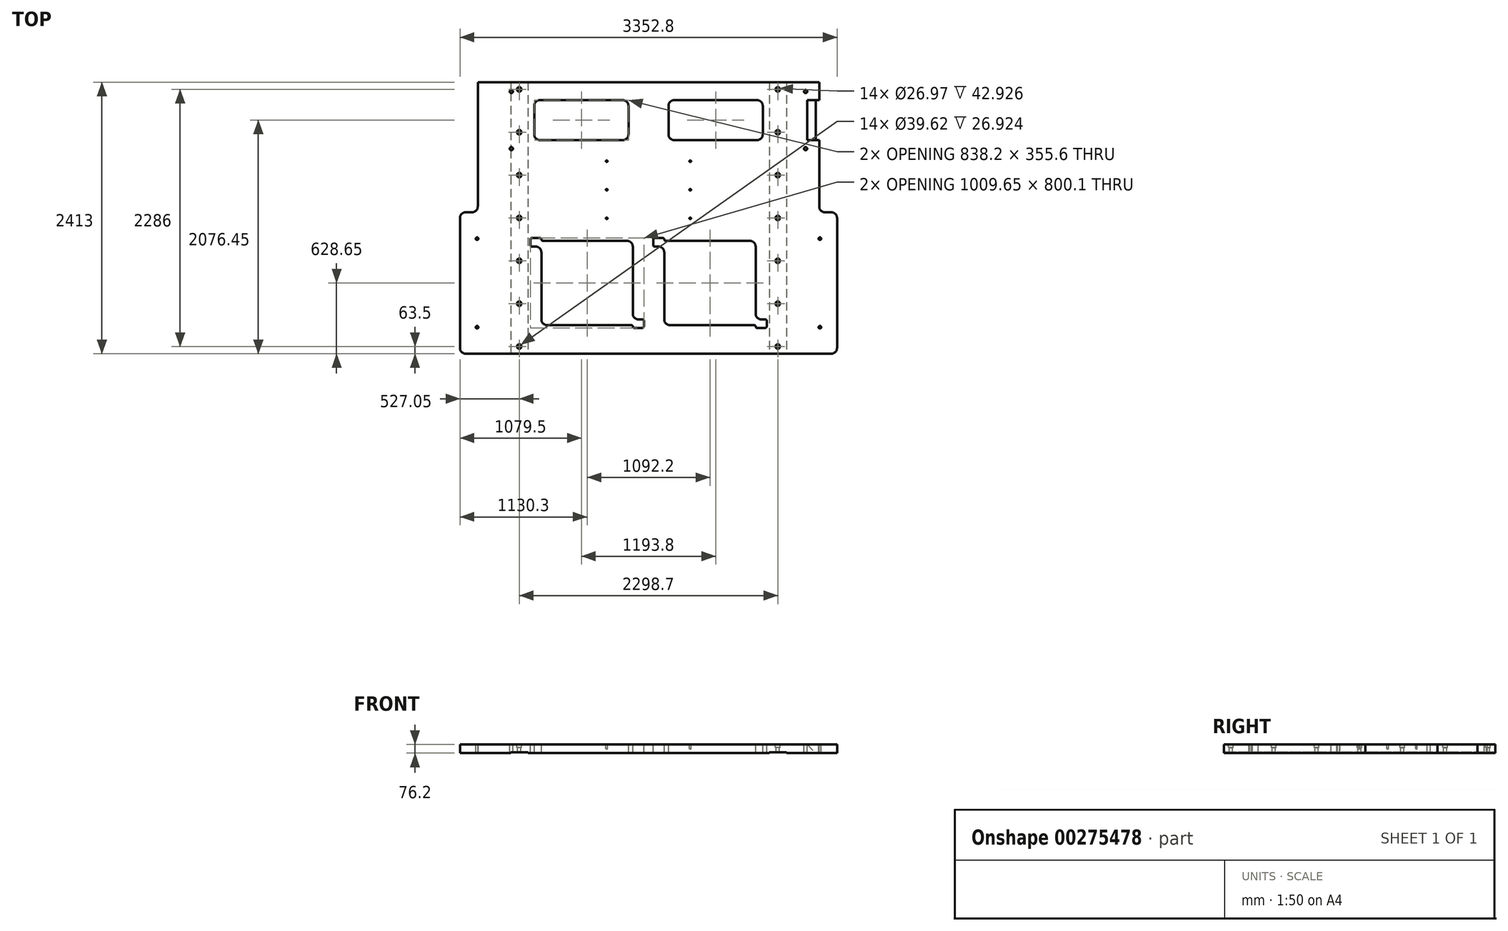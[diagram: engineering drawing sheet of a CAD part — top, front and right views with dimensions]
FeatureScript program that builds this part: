
annotation { "Feature Type Name" : "Feature", "Feature Type Description" : "" }
export const myFeature = defineFeature(function(context is Context, id is Id, definition is map)
    precondition{}
    {
        {
            var Q0;
            Q0=qCreatedBy(makeId("Top.planeOp"),FACE);
            var sketch = newSketch(context, id + "F0", { "sketchPlane" : qUnion([Q0])});
            skLineSegment(sketch, "E0.bottom", {"start": v(-1676.4, 1206.5) * mm, "end": v(1676.4, 1206.5) * mm});
            skLineSegment(sketch, "E0.top", {"start": v(-1676.4, -1206.5) * mm, "end": v(1676.4, -1206.5) * mm});
            skLineSegment(sketch, "E0.left", {"start": v(-1676.4, 1206.5) * mm, "end": v(-1676.4, -1206.5) * mm});
            skLineSegment(sketch, "E0.right", {"start": v(1676.4, 1206.5) * mm, "end": v(1676.4, -1206.5) * mm});
            skPoint(sketch, "E0.middle", {"position": v(0, 0) * mm});
            skSolve(sketch);
        }
        {
            var Q0;
            Q0 = qSketchRegion(id + "F0", true);
            extrude(context, id + "F1", {"entities" : qUnion([Q0]), "oppositeDirection" : true, "depth" : 76.2 * mm});
        }
        {
            var Q0;
            Q0=makeQuery(id+"F1.opExtrude","SWEPT_FACE",FACE,{"disambiguationData":[OSD([sQuery(id+"F0.wireOp",EDGE,"E0.top")])]});
            var sketch = newSketch(context, id + "F2", { "sketchPlane" : qUnion([Q0])});
            skLineSegment(sketch, "E1", {"start": v(0, 468.94) * mm, "end": v(0, -416.44) * mm, "construction": true});
            skLineSegment(sketch, "E2.0", {"start": v(-1676.4, -76.2) * mm, "end": v(1676.4, -76.2) * mm, "construction": true});
            skLineSegment(sketch, "E3.0", {"start": v(-1073.15, 468.94) * mm, "end": v(-1073.15, -416.44) * mm, "construction": true});
            skLineSegment(sketch, "E4.0", {"start": v(-1517.65, -69.85) * mm, "end": v(1517.65, -69.85) * mm, "construction": true});
            skLineSegment(sketch, "E5.bottom", {"start": v(-1073.15, -69.85) * mm, "end": v(-1225.55, -69.85) * mm});
            skLineSegment(sketch, "E5.top", {"start": v(-1073.15, -95.25) * mm, "end": v(-1225.55, -95.25) * mm});
            skLineSegment(sketch, "E5.left", {"start": v(-1073.15, -69.85) * mm, "end": v(-1073.15, -95.25) * mm});
            skLineSegment(sketch, "E5.right", {"start": v(-1225.55, -69.85) * mm, "end": v(-1225.55, -95.25) * mm});
            skLineSegment(sketch, "E6.MirrorCS", {"start": v(1073.15, -69.85) * mm, "end": v(1073.15, -95.25) * mm});
            skLineSegment(sketch, "E7.MirrorCS", {"start": v(1225.55, -69.85) * mm, "end": v(1225.55, -95.25) * mm});
            skLineSegment(sketch, "E8.MirrorCS", {"start": v(1073.15, -95.25) * mm, "end": v(1225.55, -95.25) * mm});
            skLineSegment(sketch, "E9.MirrorCS", {"start": v(1073.15, -69.85) * mm, "end": v(1225.55, -69.85) * mm});
            skSolve(sketch);
        }
        {
            var Q0;
            {var subQ0=sQuery(id+"F2.wireOp",EDGE,"E5.top");Q0=makeQuery(id+"F2.imprint","IMPRINT",FACE,{"disambiguationData":[TD([[makeQuery(id+"F2.imprint","IMPRINT",EDGE,{"derivedFrom":subQ0}),-1.0]])]});}
            var Q1;
            {var subQ0=sQuery(id+"F2.wireOp",EDGE,"E8.MirrorCS");Q1=makeQuery(id+"F2.imprint","IMPRINT",FACE,{"disambiguationData":[TD([[makeQuery(id+"F2.imprint","IMPRINT",EDGE,{"derivedFrom":subQ0}),1.0]])]});}
            var Q2;
            {var subQ0=sQuery(id+"F2.wireOp",EDGE,"E9.MirrorCS");Q2=makeQuery(id+"F2.imprint","IMPRINT",FACE,{"disambiguationData":[TD([[makeQuery(id+"F2.imprint","IMPRINT",EDGE,{"derivedFrom":subQ0}),-1.0]])]});}
            var Q3;
            {var subQ0=sQuery(id+"F2.wireOp",EDGE,"E5.bottom");Q3=makeQuery(id+"F2.imprint","IMPRINT",FACE,{"disambiguationData":[TD([[makeQuery(id+"F2.imprint","IMPRINT",EDGE,{"derivedFrom":subQ0}),1.0]])]});}
            extrude(context, id + "F3", {"entities" : qUnion([Q0, Q1, Q2, Q3]), "operationType" : NewBodyOperationType.REMOVE, "endBound" : BoundingType.THROUGH_ALL, "oppositeDirection" : true, "depth" : 25.4 * mm});
        }
        {
            var Q0;
            Q0=makeQuery(id+"F1.opExtrude","CAP_FACE",FACE,{"disambiguationData":[OSD([sQuery(id+"F0.wireOp",EDGE,"E0.bottom"),sQuery(id+"F0.wireOp",EDGE,"E0.top"),sQuery(id+"F0.wireOp",EDGE,"E0.left"),sQuery(id+"F0.wireOp",EDGE,"E0.right")])],"isStart":true});
            var sketch = newSketch(context, id + "F4", { "sketchPlane" : qUnion([Q0])});
            skLineSegment(sketch, "E10", {"start": v(0, 2002.4) * mm, "end": v(0, -1867.77) * mm, "construction": true});
            skLineSegment(sketch, "E11.0", {"start": v(-1517.65, 2002.4) * mm, "end": v(-1517.65, -1867.77) * mm, "construction": true});
            skLineSegment(sketch, "E12.0", {"start": v(-1676.4, -1206.5) * mm, "end": v(1676.4, -1206.5) * mm, "construction": true});
            skLineSegment(sketch, "E13.0", {"start": v(-1676.4, 50.8) * mm, "end": v(1676.4, 50.8) * mm, "construction": true});
            skLineSegment(sketch, "E14.0", {"start": v(-1682.75, 1212.85) * mm, "end": v(-1682.75, -1212.85) * mm, "construction": true});
            skLineSegment(sketch, "E14.1", {"start": v(1682.75, 1212.85) * mm, "end": v(-1682.75, 1212.85) * mm, "construction": true});
            skLineSegment(sketch, "E14.2", {"start": v(1682.75, -1212.85) * mm, "end": v(1682.75, 1212.85) * mm, "construction": true});
            skLineSegment(sketch, "E14.3", {"start": v(-1682.75, -1212.85) * mm, "end": v(1682.75, -1212.85) * mm, "construction": true});
            skLineSegment(sketch, "E15.bottom", {"start": v(-1517.65, 50.8) * mm, "end": v(-1682.75, 50.8) * mm});
            skLineSegment(sketch, "E15.top", {"start": v(-1517.65, 1212.85) * mm, "end": v(-1682.75, 1212.85) * mm});
            skLineSegment(sketch, "E15.left", {"start": v(-1517.65, 50.8) * mm, "end": v(-1517.65, 1212.85) * mm});
            skLineSegment(sketch, "E15.right", {"start": v(-1682.75, 50.8) * mm, "end": v(-1682.75, 1212.85) * mm});
            skLineSegment(sketch, "E16.MirrorCS", {"start": v(1517.65, 50.8) * mm, "end": v(1682.75, 50.8) * mm});
            skLineSegment(sketch, "E17.MirrorCS", {"start": v(1517.65, 1212.85) * mm, "end": v(1682.75, 1212.85) * mm});
            skLineSegment(sketch, "E18.MirrorCS", {"start": v(1682.75, 50.8) * mm, "end": v(1682.75, 1212.85) * mm});
            skLineSegment(sketch, "E19.MirrorCS", {"start": v(1517.65, 50.8) * mm, "end": v(1517.65, 1212.85) * mm});
            skSolve(sketch);
        }
        {
            var Q0;
            Q0 = qSketchRegion(id + "F4", true);
            extrude(context, id + "F5", {"entities" : qUnion([Q0]), "operationType" : NewBodyOperationType.REMOVE, "endBound" : BoundingType.THROUGH_ALL, "oppositeDirection" : true, "depth" : 25.4 * mm});
        }
        {
            var Q0;
            Q0=makeQuery(id+"F1.opExtrude","SWEPT_EDGE",EDGE,{"disambiguationData":[OSD([sQuery(id+"F0.wireOp",EDGE,"E0.top"),sQuery(id+"F0.wireOp",EDGE,"E0.left")])]});
            var Q1;
            Q1=makeQuery(id+"F5.boolean.opBoolean","INTERSECT",EDGE,{"derivedFrom":[makeQuery(id+"F1.opExtrude","SWEPT_FACE",FACE,{"disambiguationData":[OSD([sQuery(id+"F0.wireOp",EDGE,"E0.left")])]}),makeQuery(id+"F5.opExtrude","SWEPT_FACE",FACE,{"disambiguationData":[OSD([sQuery(id+"F4.wireOp",EDGE,"E15.bottom")])]})]});
            var Q2;
            Q2=makeQuery(id+"F5.boolean.opBoolean","COPY",EDGE,{"derivedFrom":makeQuery(id+"F5.opExtrude","SWEPT_EDGE",EDGE,{"disambiguationData":[OSD([sQuery(id+"F4.wireOp",EDGE,"E15.bottom"),sQuery(id+"F4.wireOp",EDGE,"E15.left")])]})});
            var Q3;
            Q3=makeQuery(id+"F5.boolean.opBoolean","COPY",EDGE,{"derivedFrom":makeQuery(id+"F5.opExtrude","SWEPT_EDGE",EDGE,{"disambiguationData":[OSD([sQuery(id+"F4.wireOp",EDGE,"E16.MirrorCS"),sQuery(id+"F4.wireOp",EDGE,"E19.MirrorCS")])]})});
            var Q4;
            Q4=makeQuery(id+"F5.boolean.opBoolean","INTERSECT",EDGE,{"derivedFrom":[makeQuery(id+"F1.opExtrude","SWEPT_FACE",FACE,{"disambiguationData":[OSD([sQuery(id+"F0.wireOp",EDGE,"E0.right")])]}),makeQuery(id+"F5.opExtrude","SWEPT_FACE",FACE,{"disambiguationData":[OSD([sQuery(id+"F4.wireOp",EDGE,"E16.MirrorCS")])]})]});
            var Q5;
            Q5=makeQuery(id+"F1.opExtrude","SWEPT_EDGE",EDGE,{"disambiguationData":[OSD([sQuery(id+"F0.wireOp",EDGE,"E0.top"),sQuery(id+"F0.wireOp",EDGE,"E0.right")])]});
            fillet(context, id + "F6", {"entities" : qUnion([Q0, Q1, Q2, Q3, Q4, Q5]), "radius" : 50.8 * mm, "tangentPropagation" : true, "allowEdgeOverflow" : false});
        }
        {
            var Q0;
            Q0=makeQuery(id+"F1.opExtrude","CAP_FACE",FACE,{"disambiguationData":[OSD([sQuery(id+"F0.wireOp",EDGE,"E0.bottom"),sQuery(id+"F0.wireOp",EDGE,"E0.top"),sQuery(id+"F0.wireOp",EDGE,"E0.left"),sQuery(id+"F0.wireOp",EDGE,"E0.right")])],"isStart":true});
            var sketch = newSketch(context, id + "F7", { "sketchPlane" : qUnion([Q0])});
            skLineSegment(sketch, "E20", {"start": v(0, 1658.03) * mm, "end": v(0, -1598.46) * mm, "construction": true});
            skPoint(sketch, "E20.endSnap0", {"position": v(0, -1206.5) * mm});
            skLineSegment(sketch, "E21.0", {"start": v(-1517.65, 1206.5) * mm, "end": v(1517.65, 1206.5) * mm, "construction": true});
            skLineSegment(sketch, "E22.0", {"start": v(-1517.65, 869.95) * mm, "end": v(1517.65, 869.95) * mm, "construction": true});
            skLineSegment(sketch, "E23.bottom", {"start": v(-965.2, 692.15) * mm, "end": v(-228.6, 692.15) * mm});
            skLineSegment(sketch, "E23.top", {"start": v(-965.2, 1047.75) * mm, "end": v(-228.6, 1047.75) * mm});
            skLineSegment(sketch, "E23.left", {"start": v(-1016, 742.95) * mm, "end": v(-1016, 996.95) * mm});
            skLineSegment(sketch, "E23.right", {"start": v(-177.8, 742.95) * mm, "end": v(-177.8, 996.95) * mm});
            skPoint(sketch, "E24.visualSharp", {"position": v(-1016, 1047.75) * mm});
            skArc(sketch, "E24.filletArc", {"start": v(-965.2, 1047.75) * mm, "mid": v(-1001.12, 1032.87) * mm, "end": v(-1016, 996.95) * mm});
            skPoint(sketch, "E25.visualSharp", {"position": v(-177.8, 1047.75) * mm});
            skArc(sketch, "E25.filletArc", {"start": v(-177.8, 996.95) * mm, "mid": v(-192.68, 1032.87) * mm, "end": v(-228.6, 1047.75) * mm});
            skPoint(sketch, "E26.visualSharp", {"position": v(-177.8, 692.15) * mm});
            skArc(sketch, "E26.filletArc", {"start": v(-228.6, 692.15) * mm, "mid": v(-192.68, 707.03) * mm, "end": v(-177.8, 742.95) * mm});
            skPoint(sketch, "E27.visualSharp", {"position": v(-1016, 692.15) * mm});
            skArc(sketch, "E27.filletArc", {"start": v(-1016, 742.95) * mm, "mid": v(-1001.12, 707.03) * mm, "end": v(-965.2, 692.15) * mm});
            skArc(sketch, "E28.MirrorCS", {"start": v(1016, 742.95) * mm, "mid": v(1001.12, 707.03) * mm, "end": v(965.2, 692.15) * mm});
            skArc(sketch, "E29.MirrorCS", {"start": v(228.6, 692.15) * mm, "mid": v(192.68, 707.03) * mm, "end": v(177.8, 742.95) * mm});
            skArc(sketch, "E30.MirrorCS", {"start": v(177.8, 996.95) * mm, "mid": v(192.68, 1032.87) * mm, "end": v(228.6, 1047.75) * mm});
            skArc(sketch, "E31.MirrorCS", {"start": v(965.2, 1047.75) * mm, "mid": v(1001.12, 1032.87) * mm, "end": v(1016, 996.95) * mm});
            skPoint(sketch, "E32.MirrorP", {"position": v(177.8, 1047.75) * mm});
            skPoint(sketch, "E33.MirrorP", {"position": v(177.8, 692.15) * mm});
            skLineSegment(sketch, "E34.MirrorCS", {"start": v(965.2, 692.15) * mm, "end": v(228.6, 692.15) * mm});
            skPoint(sketch, "E35.MirrorP", {"position": v(1016, 1047.75) * mm});
            skPoint(sketch, "E36.MirrorP", {"position": v(1016, 692.15) * mm});
            skLineSegment(sketch, "E37.MirrorCS", {"start": v(177.8, 742.95) * mm, "end": v(177.8, 996.95) * mm});
            skLineSegment(sketch, "E38.MirrorCS", {"start": v(1016, 742.95) * mm, "end": v(1016, 996.95) * mm});
            skLineSegment(sketch, "E39.MirrorCS", {"start": v(965.2, 1047.75) * mm, "end": v(228.6, 1047.75) * mm});
            skSolve(sketch);
        }
        {
            var Q0;
            Q0 = qSketchRegion(id + "F7", true);
            extrude(context, id + "F8", {"entities" : qUnion([Q0]), "operationType" : NewBodyOperationType.REMOVE, "endBound" : BoundingType.THROUGH_ALL, "oppositeDirection" : true, "depth" : 25.4 * mm});
        }
        {
            var Q0;
            Q0=makeQuery(id+"F1.opExtrude","CAP_FACE",FACE,{"disambiguationData":[OSD([sQuery(id+"F0.wireOp",EDGE,"E0.bottom"),sQuery(id+"F0.wireOp",EDGE,"E0.top"),sQuery(id+"F0.wireOp",EDGE,"E0.left"),sQuery(id+"F0.wireOp",EDGE,"E0.right")])],"isStart":true});
            var sketch = newSketch(context, id + "F9", { "sketchPlane" : qUnion([Q0])});
            skLineSegment(sketch, "E40", {"start": v(0, 1573.8) * mm, "end": v(0, -1474.82) * mm, "construction": true});
            skLineSegment(sketch, "E41.0", {"start": v(-1625.6, -1206.5) * mm, "end": v(1625.6, -1206.5) * mm, "construction": true});
            skLineSegment(sketch, "E42.0", {"start": v(-1625.6, -577.85) * mm, "end": v(1625.6, -577.85) * mm, "construction": true});
            skLineSegment(sketch, "E43.0", {"start": v(-952.5, 1573.8) * mm, "end": v(-952.5, -177.8) * mm, "construction": true});
            skLineSegment(sketch, "E44.0", {"start": v(-139.7, -952.5) * mm, "end": v(0, -952.5) * mm, "construction": true});
            skLineSegment(sketch, "E45.bottom", {"start": v(-901.7, -952.5) * mm, "end": v(-152.4, -952.5) * mm});
            skLineSegment(sketch, "E45.top", {"start": v(-939.8, -203.2) * mm, "end": v(-190.5, -203.2) * mm});
            skLineSegment(sketch, "E45.left", {"start": v(-952.5, -901.7) * mm, "end": v(-952.5, -304.8) * mm});
            skLineSegment(sketch, "E45.right", {"start": v(-139.7, -850.9) * mm, "end": v(-139.7, -254) * mm});
            skLineSegment(sketch, "E46.bottom", {"start": v(-1038.22, -177.8) * mm, "end": v(-965.2, -177.8) * mm});
            skLineSegment(sketch, "E46.top", {"start": v(-1038.22, -254) * mm, "end": v(-1003.3, -254) * mm});
            skLineSegment(sketch, "E46.left", {"start": v(-1050.92, -190.5) * mm, "end": v(-1050.92, -241.3) * mm});
            skLineSegment(sketch, "E46.right", {"start": v(-952.5, -190.5) * mm, "end": v(-952.5, -190.5) * mm});
            skLineSegment(sketch, "E47", {"start": v(-546.1, -203.2) * mm, "end": v(-546.1, 0) * mm, "construction": true});
            skLineSegment(sketch, "E48.bottom", {"start": v(-53.97, -977.9) * mm, "end": v(-127, -977.9) * mm});
            skLineSegment(sketch, "E48.top", {"start": v(-53.97, -901.7) * mm, "end": v(-88.9, -901.7) * mm});
            skLineSegment(sketch, "E48.left", {"start": v(-41.27, -965.2) * mm, "end": v(-41.27, -914.4) * mm});
            skLineSegment(sketch, "E48.right", {"start": v(-139.7, -965.2) * mm, "end": v(-139.7, -965.2) * mm});
            skPoint(sketch, "E49.orphan", {"position": v(-952.5, -203.2) * mm});
            skLineSegment(sketch, "E50.trimOffspring", {"start": v(-139.7, -1004.26) * mm, "end": v(-139.7, -1474.82) * mm, "construction": true});
            skLineSegment(sketch, "E51.trimOffspring", {"start": v(-139.7, -952.5) * mm, "end": v(1625.6, -952.5) * mm, "construction": true});
            skPoint(sketch, "E52.visualSharp", {"position": v(-952.5, -952.5) * mm});
            skArc(sketch, "E52.filletArc", {"start": v(-952.5, -901.7) * mm, "mid": v(-937.62, -937.62) * mm, "end": v(-901.7, -952.5) * mm});
            skPoint(sketch, "E53.visualSharp", {"position": v(-139.7, -203.2) * mm});
            skArc(sketch, "E53.filletArc", {"start": v(-139.7, -254) * mm, "mid": v(-154.58, -218.08) * mm, "end": v(-190.5, -203.2) * mm});
            skPoint(sketch, "E54.visualSharp", {"position": v(-139.7, -901.7) * mm});
            skArc(sketch, "E54.filletArc", {"start": v(-139.7, -850.9) * mm, "mid": v(-124.82, -886.82) * mm, "end": v(-88.9, -901.7) * mm});
            skPoint(sketch, "E55.visualSharp", {"position": v(-952.5, -254) * mm});
            skArc(sketch, "E55.filletArc", {"start": v(-952.5, -304.8) * mm, "mid": v(-967.38, -268.88) * mm, "end": v(-1003.3, -254) * mm});
            skPoint(sketch, "E56.visualSharp", {"position": v(-1050.92, -254) * mm});
            skArc(sketch, "E56.filletArc", {"start": v(-1050.92, -241.3) * mm, "mid": v(-1047.2, -250.28) * mm, "end": v(-1038.22, -254) * mm});
            skPoint(sketch, "E57.visualSharp", {"position": v(-1050.92, -177.8) * mm});
            skArc(sketch, "E57.filletArc", {"start": v(-1038.22, -177.8) * mm, "mid": v(-1047.2, -181.52) * mm, "end": v(-1050.92, -190.5) * mm});
            skPoint(sketch, "E58.visualSharp", {"position": v(-952.5, -177.8) * mm});
            skArc(sketch, "E58.filletArc", {"start": v(-952.5, -190.5) * mm, "mid": v(-956.22, -181.52) * mm, "end": v(-965.2, -177.8) * mm});
            skArc(sketch, "E59.filletArc", {"start": v(-952.5, -190.5) * mm, "mid": v(-948.78, -199.48) * mm, "end": v(-939.8, -203.2) * mm});
            skPoint(sketch, "E60.visualSharp", {"position": v(-41.27, -901.7) * mm});
            skArc(sketch, "E60.filletArc", {"start": v(-41.27, -914.4) * mm, "mid": v(-45, -905.42) * mm, "end": v(-53.97, -901.7) * mm});
            skPoint(sketch, "E61.visualSharp", {"position": v(-41.27, -977.9) * mm});
            skArc(sketch, "E61.filletArc", {"start": v(-53.97, -977.9) * mm, "mid": v(-45, -974.18) * mm, "end": v(-41.27, -965.2) * mm});
            skPoint(sketch, "E62.visualSharp", {"position": v(-139.7, -977.9) * mm});
            skArc(sketch, "E62.filletArc", {"start": v(-139.7, -965.2) * mm, "mid": v(-135.98, -974.18) * mm, "end": v(-127, -977.9) * mm});
            skPoint(sketch, "E63.visualSharp", {"position": v(-139.7, -952.5) * mm});
            skArc(sketch, "E63.filletArc", {"start": v(-139.7, -965.2) * mm, "mid": v(-143.42, -956.22) * mm, "end": v(-152.4, -952.5) * mm});
            skPoint(sketch, "E64.1.0.0", {"position": v(41.28, -177.8) * mm});
            skPoint(sketch, "E64.1.0.1", {"position": v(952.5, -203.2) * mm});
            skLineSegment(sketch, "E64.1.0.2", {"start": v(139.7, -901.7) * mm, "end": v(139.7, -304.8) * mm});
            skPoint(sketch, "E64.1.0.3", {"position": v(41.28, -254) * mm});
            skLineSegment(sketch, "E64.1.0.4", {"start": v(190.5, -952.5) * mm, "end": v(939.8, -952.5) * mm});
            skLineSegment(sketch, "E64.1.0.5", {"start": v(152.4, -203.2) * mm, "end": v(901.7, -203.2) * mm});
            skLineSegment(sketch, "E64.1.0.6", {"start": v(952.5, -850.9) * mm, "end": v(952.5, -254) * mm});
            skPoint(sketch, "E64.1.0.7", {"position": v(139.7, -952.5) * mm});
            skPoint(sketch, "E64.1.0.8", {"position": v(952.5, -901.7) * mm});
            skPoint(sketch, "E64.1.0.9", {"position": v(952.5, -977.9) * mm});
            skPoint(sketch, "E64.1.0.10", {"position": v(1050.93, -977.9) * mm});
            skPoint(sketch, "E64.1.0.11", {"position": v(139.7, -177.8) * mm});
            skPoint(sketch, "E64.1.0.12", {"position": v(139.7, -254) * mm});
            skPoint(sketch, "E64.1.0.13", {"position": v(1050.93, -901.7) * mm});
            skArc(sketch, "E64.1.0.14", {"start": v(952.5, -254) * mm, "mid": v(937.62, -218.08) * mm, "end": v(901.7, -203.2) * mm});
            skArc(sketch, "E64.1.0.15", {"start": v(952.5, -850.9) * mm, "mid": v(967.38, -886.82) * mm, "end": v(1003.3, -901.7) * mm});
            skLineSegment(sketch, "E64.1.0.16", {"start": v(952.5, -952.5) * mm, "end": v(1092.2, -952.5) * mm, "construction": true});
            skPoint(sketch, "E64.1.0.17", {"position": v(139.7, -203.2) * mm});
            skPoint(sketch, "E64.1.0.18", {"position": v(952.5, -952.5) * mm});
            skLineSegment(sketch, "E64.1.0.19", {"start": v(1038.23, -977.9) * mm, "end": v(965.2, -977.9) * mm});
            skArc(sketch, "E64.1.0.20", {"start": v(139.7, -304.8) * mm, "mid": v(124.82, -268.88) * mm, "end": v(88.9, -254) * mm});
            skPoint(sketch, "E64.1.0.21", {"position": v(139.7, -203.2) * mm});
            skArc(sketch, "E64.1.0.22", {"start": v(139.7, -901.7) * mm, "mid": v(154.58, -937.62) * mm, "end": v(190.5, -952.5) * mm});
            skArc(sketch, "E64.1.0.23", {"start": v(1038.23, -977.9) * mm, "mid": v(1047.2, -974.18) * mm, "end": v(1050.93, -965.2) * mm});
            skLineSegment(sketch, "E64.1.0.24", {"start": v(53.98, -254) * mm, "end": v(88.9, -254) * mm});
            skLineSegment(sketch, "E64.1.0.25", {"start": v(53.98, -177.8) * mm, "end": v(127, -177.8) * mm});
            skLineSegment(sketch, "E64.1.0.26", {"start": v(41.28, -190.5) * mm, "end": v(41.28, -241.3) * mm});
            skArc(sketch, "E64.1.0.27", {"start": v(53.98, -177.8) * mm, "mid": v(45, -181.52) * mm, "end": v(41.28, -190.5) * mm});
            skLineSegment(sketch, "E64.1.0.28", {"start": v(1050.93, -965.2) * mm, "end": v(1050.93, -914.4) * mm});
            skLineSegment(sketch, "E64.1.0.29", {"start": v(1038.23, -901.7) * mm, "end": v(1003.3, -901.7) * mm});
            skArc(sketch, "E64.1.0.30", {"start": v(41.28, -241.3) * mm, "mid": v(45, -250.28) * mm, "end": v(53.98, -254) * mm});
            skArc(sketch, "E64.1.0.31", {"start": v(952.5, -965.2) * mm, "mid": v(948.78, -956.22) * mm, "end": v(939.8, -952.5) * mm});
            skArc(sketch, "E64.1.0.32", {"start": v(952.5, -965.2) * mm, "mid": v(956.22, -974.18) * mm, "end": v(965.2, -977.9) * mm});
            skArc(sketch, "E64.1.0.33", {"start": v(1050.93, -914.4) * mm, "mid": v(1047.2, -905.42) * mm, "end": v(1038.23, -901.7) * mm});
            skArc(sketch, "E64.1.0.34", {"start": v(139.7, -190.5) * mm, "mid": v(135.98, -181.52) * mm, "end": v(127, -177.8) * mm});
            skArc(sketch, "E64.1.0.35", {"start": v(139.7, -190.5) * mm, "mid": v(143.42, -199.48) * mm, "end": v(152.4, -203.2) * mm});
            skLineSegment(sketch, "E64.direction1", {"start": v(-952.5, -952.5) * mm, "end": v(139.7, -952.5) * mm, "construction": true});
            skSolve(sketch);
        }
        {
            var Q0;
            Q0 = qSketchRegion(id + "F9", true);
            extrude(context, id + "F10", {"entities" : qUnion([Q0]), "operationType" : NewBodyOperationType.REMOVE, "endBound" : BoundingType.THROUGH_ALL, "oppositeDirection" : true, "depth" : 25.4 * mm});
        }
        {
            var Q0;
            Q0=makeQuery(id+"F1.opExtrude","SWEPT_FACE",FACE,{"disambiguationData":[OSD([sQuery(id+"F0.wireOp",EDGE,"E0.bottom")])]});
            cPlane(context, id + "F11", {"entities" : qUnion([Q0]), "cplaneType" : CPlaneType.OFFSET, "offset" : 336.55 * mm, "oppositeDirection" : true, "width" : 152.4 * mm, "height" : 152.4 * mm});
        }
        {
            var Q0;
            Q0=qCreatedBy(id+"F11.planeOp",FACE);
            var sketch = newSketch(context, id + "F12", { "sketchPlane" : qUnion([Q0])});
            skLineSegment(sketch, "E65", {"start": v(0, 694.36) * mm, "end": v(0, -636.94) * mm, "construction": true});
            skLineSegment(sketch, "E66.0", {"start": v(-1409.7, 694.36) * mm, "end": v(-1409.7, 0) * mm, "construction": true});
            skLineSegment(sketch, "E67.0", {"start": v(-1225.55, -76.2) * mm, "end": v(-1409.7, -76.2) * mm, "construction": true});
            skLineSegment(sketch, "E68.top", {"start": v(-1409.7, 0) * mm, "end": v(-1485.91, 0) * mm});
            skLineSegment(sketch, "E69", {"start": v(-1409.7, 0) * mm, "end": v(-1485.91, -76.2) * mm});
            skLineSegment(sketch, "E70.trimOffspring", {"start": v(-1409.7, -76.2) * mm, "end": v(-1409.7, -636.94) * mm, "construction": true});
            skLineSegment(sketch, "E71.trimOffspring", {"start": v(-1485.91, -76.2) * mm, "end": v(-1517.65, -76.2) * mm, "construction": true});
            skLineSegment(sketch, "E72.bottom", {"start": v(-1485.91, 0) * mm, "end": v(-1554.1, 0) * mm});
            skLineSegment(sketch, "E72.top", {"start": v(-1485.91, -76.2) * mm, "end": v(-1554.1, -76.2) * mm});
            skLineSegment(sketch, "E72.right", {"start": v(-1554.1, 0) * mm, "end": v(-1554.1, -76.2) * mm});
            skSolve(sketch);
        }
        {
            var Q0;
            Q0 = qSketchRegion(id + "F12", true);
            extrude(context, id + "F13", {"entities" : qUnion([Q0]), "operationType" : NewBodyOperationType.REMOVE, "endBound" : BoundingType.SYMMETRIC, "oppositeDirection" : true, "depth" : 355.6 * mm});
        }
        {
            var Q0;
            Q0=makeQuery(id+"F1.opExtrude","CAP_FACE",FACE,{"disambiguationData":[OSD([sQuery(id+"F0.wireOp",EDGE,"E0.bottom"),sQuery(id+"F0.wireOp",EDGE,"E0.top"),sQuery(id+"F0.wireOp",EDGE,"E0.left"),sQuery(id+"F0.wireOp",EDGE,"E0.right")])],"isStart":true});
            var sketch = newSketch(context, id + "F14", { "sketchPlane" : qUnion([Q0])});
            skLineSegment(sketch, "E73", {"start": v(0, 1417.77) * mm, "end": v(0, -1448.45) * mm, "construction": true});
            skLineSegment(sketch, "E74", {"start": v(-177.8, 869.95) * mm, "end": v(-2109.21, 869.95) * mm, "construction": true});
            skLineSegment(sketch, "E75.0", {"start": v(-177.8, 250.7) * mm, "end": v(-2109.21, 250.7) * mm, "construction": true});
            skLineSegment(sketch, "E76.0", {"start": v(-177.8, -3.3) * mm, "end": v(-2109.21, -3.3) * mm, "construction": true});
            skLineSegment(sketch, "E77.0", {"start": v(-177.8, 504.7) * mm, "end": v(-2109.21, 504.7) * mm, "construction": true});
            skLineSegment(sketch, "E78.0", {"start": v(-371.35, 1417.77) * mm, "end": v(-371.35, -1448.45) * mm, "construction": true});
            skPoint(sketch, "E79", {"position": v(-371.35, 504.7) * mm});
            skPoint(sketch, "E80", {"position": v(-371.35, 250.7) * mm});
            skPoint(sketch, "E81", {"position": v(-371.35, -3.3) * mm});
            skPoint(sketch, "E82.MirrorP", {"position": v(371.35, 504.7) * mm});
            skPoint(sketch, "E83.MirrorP", {"position": v(371.35, 250.7) * mm});
            skPoint(sketch, "E84.MirrorP", {"position": v(371.35, -3.3) * mm});
            skSolve(sketch);
        }
        {
            var Q0;
            Q0=sQuery(id+"F14.wireOp",VERTEX,"E79");
            var Q1;
            Q1=sQuery(id+"F14.wireOp",VERTEX,"E80");
            var Q2;
            Q2=sQuery(id+"F14.wireOp",VERTEX,"E81");
            var Q3;
            Q3=sQuery(id+"F14.wireOp",VERTEX,"E82.MirrorP");
            var Q4;
            Q4=sQuery(id+"F14.wireOp",VERTEX,"E83.MirrorP");
            var Q5;
            Q5=sQuery(id+"F14.wireOp",VERTEX,"E84.MirrorP");
            var Q6;
            Q6=makeQuery(id+"F1.opExtrude","SWEPT_BODY",BODY,{"disambiguationData":[OSD([sQuery(id+"F0.wireOp",EDGE,"E0.bottom"),sQuery(id+"F0.wireOp",EDGE,"E0.top"),sQuery(id+"F0.wireOp",EDGE,"E0.left"),sQuery(id+"F0.wireOp",EDGE,"E0.right")])]});
            hole(context, id + "F15", {"style" : HoleStyle.SIMPLE, "endStyle" : HoleEndStyle.BLIND, "standardTappedOrClearance" : lookupTablePath({ "standard" : "ANSI", "engagement" : "75%", "pitch" : "11 tpi", "size" : "5/8", "type" : "Tapped" }), "standardBlindInLast" : lookupTablePath({ "standard" : "ANSI", "engagement" : "75%", "pitch" : "11 tpi", "size" : "5/8", "type" : "Tapped" }), "holeDiameter" : 13.5 * mm, "showTappedDepth" : true, "holeDepth" : 38.1 * mm, "tappedDepth" : 31.17 * mm, "tapClearance" : 3, "startFromSketch" : true, "locations" : qUnion([Q0, Q1, Q2, Q3, Q4, Q5]), "scope" : qUnion([Q6]), "majorDiameter" : 15.88 * mm});
        }
        {
            var Q0;
            Q0=makeQuery(id+"F1.opExtrude","CAP_FACE",FACE,{"disambiguationData":[OSD([sQuery(id+"F0.wireOp",EDGE,"E0.bottom"),sQuery(id+"F0.wireOp",EDGE,"E0.top"),sQuery(id+"F0.wireOp",EDGE,"E0.left"),sQuery(id+"F0.wireOp",EDGE,"E0.right")])],"isStart":true});
            var sketch = newSketch(context, id + "F16", { "sketchPlane" : qUnion([Q0])});
            skLineSegment(sketch, "E85", {"start": v(0, 1443.57) * mm, "end": v(0, -1540.72) * mm, "construction": true});
            skLineSegment(sketch, "E86.0", {"start": v(-1149.35, 1443.57) * mm, "end": v(-1149.35, -1540.72) * mm, "construction": true});
            skLineSegment(sketch, "E87.0", {"start": v(-1625.6, -1206.5) * mm, "end": v(1625.6, -1206.5) * mm, "construction": true});
            skLineSegment(sketch, "E88.0", {"start": v(-1625.6, -1143) * mm, "end": v(1625.6, -1143) * mm, "construction": true});
            skPoint(sketch, "E89", {"position": v(-1149.35, -1143) * mm});
            skPoint(sketch, "E90.0.1.0", {"position": v(-1149.35, -762) * mm});
            skPoint(sketch, "E90.0.2.0", {"position": v(-1149.35, -381) * mm});
            skPoint(sketch, "E90.0.3.0", {"position": v(-1149.35, 0) * mm});
            skPoint(sketch, "E90.0.4.0", {"position": v(-1149.35, 381) * mm});
            skPoint(sketch, "E90.0.5.0", {"position": v(-1149.35, 762) * mm});
            skPoint(sketch, "E90.0.6.0", {"position": v(-1149.35, 1143) * mm});
            skPoint(sketch, "E90.1.0.0", {"position": v(1149.35, -1143) * mm});
            skPoint(sketch, "E90.1.1.0", {"position": v(1149.35, -762) * mm});
            skPoint(sketch, "E90.1.2.0", {"position": v(1149.35, -381) * mm});
            skPoint(sketch, "E90.1.3.0", {"position": v(1149.35, 0) * mm});
            skPoint(sketch, "E90.1.4.0", {"position": v(1149.35, 381) * mm});
            skPoint(sketch, "E90.1.5.0", {"position": v(1149.35, 762) * mm});
            skPoint(sketch, "E90.1.6.0", {"position": v(1149.35, 1143) * mm});
            skLineSegment(sketch, "E90.direction1", {"start": v(-1149.35, -1143) * mm, "end": v(1149.35, -1143) * mm, "construction": true});
            skLineSegment(sketch, "E90.direction2", {"start": v(-1149.35, -1143) * mm, "end": v(-1149.35, -762) * mm, "construction": true});
            skSolve(sketch);
        }
        {
            var Q0;
            Q0=sQuery(id+"F16.wireOp",VERTEX,"E89");
            var Q1;
            Q1=sQuery(id+"F16.wireOp",VERTEX,"E90.0.1.0");
            var Q2;
            Q2=sQuery(id+"F16.wireOp",VERTEX,"E90.0.2.0");
            var Q3;
            Q3=sQuery(id+"F16.wireOp",VERTEX,"E90.0.3.0");
            var Q4;
            Q4=sQuery(id+"F16.wireOp",VERTEX,"E90.0.4.0");
            var Q5;
            Q5=sQuery(id+"F16.wireOp",VERTEX,"E90.0.5.0");
            var Q6;
            Q6=sQuery(id+"F16.wireOp",VERTEX,"E90.0.6.0");
            var Q7;
            Q7=sQuery(id+"F16.wireOp",VERTEX,"E90.1.6.0");
            var Q8;
            Q8=sQuery(id+"F16.wireOp",VERTEX,"E90.1.5.0");
            var Q9;
            Q9=sQuery(id+"F16.wireOp",VERTEX,"E90.1.4.0");
            var Q10;
            Q10=sQuery(id+"F16.wireOp",VERTEX,"E90.1.3.0");
            var Q11;
            Q11=sQuery(id+"F16.wireOp",VERTEX,"E90.1.2.0");
            var Q12;
            Q12=sQuery(id+"F16.wireOp",VERTEX,"E90.1.1.0");
            var Q13;
            Q13=sQuery(id+"F16.wireOp",VERTEX,"E90.1.0.0");
            var Q14;
            Q14=makeQuery(id+"F1.opExtrude","SWEPT_BODY",BODY,{"disambiguationData":[OSD([sQuery(id+"F0.wireOp",EDGE,"E0.bottom"),sQuery(id+"F0.wireOp",EDGE,"E0.top"),sQuery(id+"F0.wireOp",EDGE,"E0.left"),sQuery(id+"F0.wireOp",EDGE,"E0.right")])]});
            hole(context, id + "F17", {"style" : HoleStyle.C_BORE, "endStyle" : HoleEndStyle.THROUGH, "holeDiameter" : 26.97 * mm, "cBoreDiameter" : 39.62 * mm, "cBoreDepth" : 26.92 * mm, "tappedDepth" : 31.17 * mm, "tapClearance" : 3, "startFromSketch" : true, "locations" : qUnion([Q0, Q1, Q2, Q3, Q4, Q5, Q6, Q7, Q8, Q9, Q10, Q11, Q12, Q13]), "scope" : qUnion([Q14])});
        }
        {
            var Q0;
            Q0=makeQuery(id+"F1.opExtrude","CAP_FACE",FACE,{"disambiguationData":[OSD([sQuery(id+"F0.wireOp",EDGE,"E0.bottom"),sQuery(id+"F0.wireOp",EDGE,"E0.top"),sQuery(id+"F0.wireOp",EDGE,"E0.left"),sQuery(id+"F0.wireOp",EDGE,"E0.right")])],"isStart":true});
            var sketch = newSketch(context, id + "F18", { "sketchPlane" : qUnion([Q0])});
            skLineSegment(sketch, "E91", {"start": v(0, 1491.37) * mm, "end": v(0, -1763.18) * mm, "construction": true});
            skLineSegment(sketch, "E92.0", {"start": v(-1524, 1491.37) * mm, "end": v(-1524, -1763.18) * mm, "construction": true});
            skLineSegment(sketch, "E93.0", {"start": v(-1625.6, -1206.5) * mm, "end": v(1625.6, -1206.5) * mm, "construction": true});
            skLineSegment(sketch, "E94.0", {"start": v(-1625.6, -577.85) * mm, "end": v(1625.6, -577.85) * mm, "construction": true});
            skLineSegment(sketch, "E95.0", {"start": v(-1625.6, -971.55) * mm, "end": v(1625.6, -971.55) * mm, "construction": true});
            skLineSegment(sketch, "E96.0", {"start": v(-1625.6, -184.15) * mm, "end": v(1625.6, -184.15) * mm, "construction": true});
            skPoint(sketch, "E97", {"position": v(-1524, -184.15) * mm});
            skPoint(sketch, "E98", {"position": v(-1524, -971.55) * mm});
            skPoint(sketch, "E99.MirrorP", {"position": v(1524, -184.15) * mm});
            skPoint(sketch, "E100.MirrorP", {"position": v(1524, -971.55) * mm});
            skSolve(sketch);
        }
        {
            var Q0;
            Q0=sQuery(id+"F18.wireOp",VERTEX,"E97");
            var Q1;
            Q1=sQuery(id+"F18.wireOp",VERTEX,"E98");
            var Q2;
            Q2=sQuery(id+"F18.wireOp",VERTEX,"E99.MirrorP");
            var Q3;
            Q3=sQuery(id+"F18.wireOp",VERTEX,"E100.MirrorP");
            var Q4;
            Q4=makeQuery(id+"F1.opExtrude","SWEPT_BODY",BODY,{"disambiguationData":[OSD([sQuery(id+"F0.wireOp",EDGE,"E0.bottom"),sQuery(id+"F0.wireOp",EDGE,"E0.top"),sQuery(id+"F0.wireOp",EDGE,"E0.left"),sQuery(id+"F0.wireOp",EDGE,"E0.right")])]});
            hole(context, id + "F19", {"style" : HoleStyle.SIMPLE, "endStyle" : HoleEndStyle.THROUGH, "standardTappedOrClearance" : lookupTablePath({ "standard" : "ANSI", "engagement" : "75%", "pitch" : "8 tpi", "size" : "1", "type" : "Tapped" }), "standardBlindInLast" : lookupTablePath({ "standard" : "ANSI", "engagement" : "75%", "pitch" : "8 tpi", "size" : "1", "type" : "Tapped" }), "holeDiameter" : 22.22 * mm, "showTappedDepth" : true, "tappedDepth" : 31.17 * mm, "tapClearance" : 3, "startFromSketch" : true, "locations" : qUnion([Q0, Q1, Q2, Q3]), "scope" : qUnion([Q4]), "majorDiameter" : 25.4 * mm});
        }
        {
            var Q0;
            Q0=makeQuery(id+"F1.opExtrude","CAP_FACE",FACE,{"disambiguationData":[OSD([sQuery(id+"F0.wireOp",EDGE,"E0.bottom"),sQuery(id+"F0.wireOp",EDGE,"E0.top"),sQuery(id+"F0.wireOp",EDGE,"E0.left"),sQuery(id+"F0.wireOp",EDGE,"E0.right")])],"isStart":true});
            var sketch = newSketch(context, id + "F20", { "sketchPlane" : qUnion([Q0])});
            skLineSegment(sketch, "E101", {"start": v(0, 1609.78) * mm, "end": v(0, -1637.77) * mm, "construction": true});
            skLineSegment(sketch, "E102.0", {"start": v(-1517.65, 1206.5) * mm, "end": v(1517.65, 1206.5) * mm, "construction": true});
            skLineSegment(sketch, "E103.0", {"start": v(1397, 1609.78) * mm, "end": v(1397, -1637.77) * mm, "construction": true});
            skLineSegment(sketch, "E104.0", {"start": v(-1517.65, 869.95) * mm, "end": v(1517.65, 869.95) * mm, "construction": true});
            skLineSegment(sketch, "E105.0", {"start": v(-1517.65, 615.95) * mm, "end": v(1517.65, 615.95) * mm, "construction": true});
            skPoint(sketch, "E106", {"position": v(1397, 615.95) * mm});
            skPoint(sketch, "E107.MirrorP", {"position": v(1397, 1123.95) * mm});
            skSolve(sketch);
        }
        {
            var Q0;
            Q0=sQuery(id+"F20.wireOp",VERTEX,"E107.MirrorP");
            var Q1;
            Q1=sQuery(id+"F20.wireOp",VERTEX,"E106");
            var Q2;
            Q2=makeQuery(id+"F1.opExtrude","SWEPT_BODY",BODY,{"disambiguationData":[OSD([sQuery(id+"F0.wireOp",EDGE,"E0.bottom"),sQuery(id+"F0.wireOp",EDGE,"E0.top"),sQuery(id+"F0.wireOp",EDGE,"E0.left"),sQuery(id+"F0.wireOp",EDGE,"E0.right")])]});
            hole(context, id + "F21", {"style" : HoleStyle.SIMPLE, "endStyle" : HoleEndStyle.THROUGH, "standardTappedOrClearance" : lookupTablePath({ "standard" : "ANSI", "engagement" : "75%", "pitch" : "7 tpi", "size" : "1 1/4", "type" : "Tapped" }), "standardBlindInLast" : lookupTablePath({ "standard" : "ANSI", "engagement" : "75%", "pitch" : "7 tpi", "size" : "1 1/4", "type" : "Tapped" }), "holeDiameter" : 28.18 * mm, "showTappedDepth" : true, "tappedDepth" : 31.17 * mm, "tapClearance" : 3, "startFromSketch" : true, "locations" : qUnion([Q0, Q1]), "scope" : qUnion([Q2]), "majorDiameter" : 31.75 * mm});
        }
        {
            var Q0;
            {var subQ4=sQuery(id+"F0.wireOp",EDGE,"E0.bottom");Q0=makeQuery(id+"F20.imprint","IMPRINT",FACE,{"disambiguationData":[TD([[makeQuery(id+"F20.imprint","IMPRINT",EDGE,{"derivedFrom":makeQuery(id+"F1.opExtrude","CAP_EDGE",EDGE,{"disambiguationData":[OSD([subQ4])],"isStart":true})}),-1.0]])]});}
            var sketch = newSketch(context, id + "F22", { "sketchPlane" : qUnion([Q0])});
            skLineSegment(sketch, "E108.0", {"start": v(0, 1609.78) * mm, "end": v(0, -1637.77) * mm, "construction": true});
            skLineSegment(sketch, "E109.0", {"start": v(1397, 1609.78) * mm, "end": v(1397, -1637.77) * mm, "construction": true});
            skLineSegment(sketch, "E110.0", {"start": v(-1517.65, 869.95) * mm, "end": v(1517.65, 869.95) * mm, "construction": true});
            skLineSegment(sketch, "E111.0", {"start": v(-1517.65, 615.95) * mm, "end": v(1517.65, 615.95) * mm, "construction": true});
            skLineSegment(sketch, "E112.0", {"start": v(-1219.2, 1609.78) * mm, "end": v(-1219.2, -1637.77) * mm, "construction": true});
            skPoint(sketch, "E113", {"position": v(-1219.2, 615.95) * mm});
            skPoint(sketch, "E114.MirrorP", {"position": v(-1219.2, 1123.95) * mm});
            skSolve(sketch);
        }
        {
            var Q0;
            Q0=sQuery(id+"F22.wireOp",VERTEX,"E114.MirrorP");
            var Q1;
            Q1=sQuery(id+"F22.wireOp",VERTEX,"E113");
            var Q2;
            Q2=makeQuery(id+"F1.opExtrude","SWEPT_BODY",BODY,{"disambiguationData":[OSD([sQuery(id+"F0.wireOp",EDGE,"E0.bottom"),sQuery(id+"F0.wireOp",EDGE,"E0.top"),sQuery(id+"F0.wireOp",EDGE,"E0.left"),sQuery(id+"F0.wireOp",EDGE,"E0.right")])]});
            hole(context, id + "F23", {"style" : HoleStyle.SIMPLE, "endStyle" : HoleEndStyle.THROUGH, "standardTappedOrClearance" : lookupTablePath({ "standard" : "ANSI", "engagement" : "75%", "pitch" : "7 tpi", "size" : "1 1/4", "type" : "Tapped" }), "standardBlindInLast" : lookupTablePath({ "standard" : "ANSI", "engagement" : "75%", "pitch" : "7 tpi", "size" : "1 1/4", "type" : "Tapped" }), "holeDiameter" : 28.18 * mm, "showTappedDepth" : true, "tappedDepth" : 31.17 * mm, "tapClearance" : 3, "startFromSketch" : true, "locations" : qUnion([Q0, Q1]), "scope" : qUnion([Q2]), "majorDiameter" : 31.75 * mm});
        }
    });
